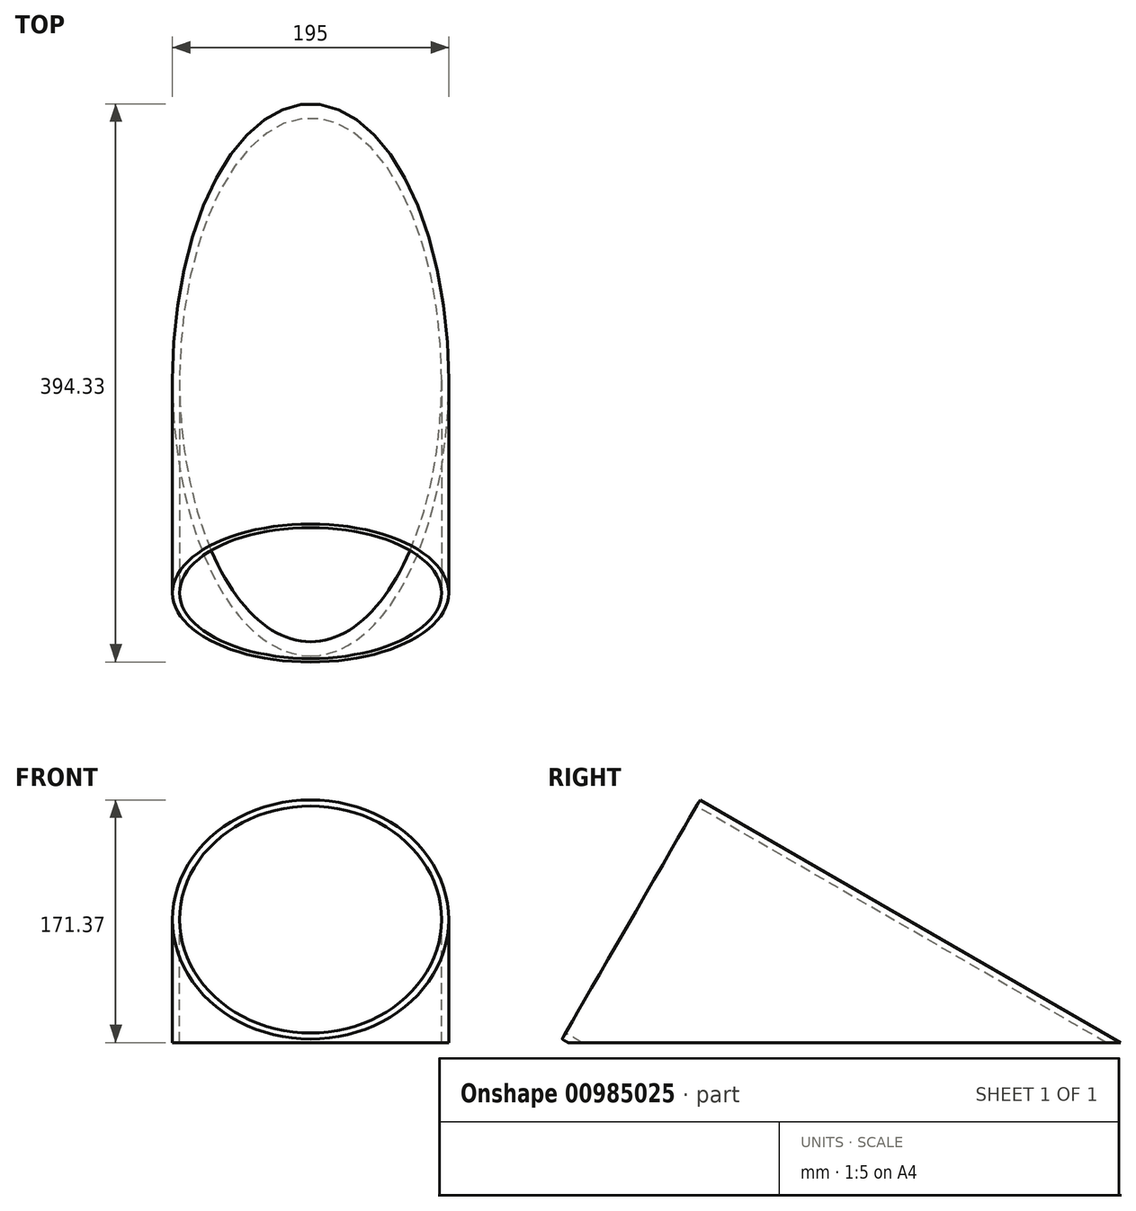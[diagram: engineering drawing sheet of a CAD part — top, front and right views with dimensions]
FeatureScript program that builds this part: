
annotation { "Feature Type Name" : "Feature", "Feature Type Description" : "" }
export const myFeature = defineFeature(function(context is Context, id is Id, definition is map)
    precondition{}
    {
        {
            var Q0;
            Q0=qCreatedBy(makeId("Top.planeOp"),FACE);
            var sketch = newSketch(context, id + "F0", { "sketchPlane" : qUnion([Q0])});
            skLineSegment(sketch, "E0", {"start": v(-54.49, 0) * mm, "end": v(52.75, 0) * mm});
            skSolve(sketch);
        }
        {
            var Q0;
            Q0=qCreatedBy(makeId("Top.planeOp"),FACE);
            var Q1;
            Q1=sQuery(id+"F0.wireOp",EDGE,"E0");
            cPlane(context, id + "F1", {"entities" : qUnion([Q0, Q1]), "cplaneType" : CPlaneType.LINE_ANGLE, "offset" : 25 * mm, "angle" : 60 * degree, "width" : 150 * mm, "height" : 150 * mm});
        }
        {
            var Q0;
            Q0=qCreatedBy(id+"F1.planeOp",FACE);
            var sketch = newSketch(context, id + "F2", { "sketchPlane" : qUnion([Q0])});
            skCircle(sketch, "E1", {"center": v(0, 97.5) * mm, "radius": 97.5 * mm});
            skCircle(sketch, "E2", {"center": v(0, 97.5) * mm, "radius": 92.5 * mm});
            skLineSegment(sketch, "E3", {"start": v(0, 0) * mm, "end": v(0, 97.5) * mm});
            skSolve(sketch);
        }
        {
            var Q0;
            Q0=makeQuery(id+"F2.imprint","IMPRINT",FACE,{"disambiguationData":[TD([[makeQuery(id+"F2.imprint","IMPRINT",EDGE,{"derivedFrom":sQuery(id+"F2.wireOp",EDGE,"E1")}),1.0]])]});
            var Q1;
            Q1=qCreatedBy(makeId("Top.planeOp"),FACE);
            extrude(context, id + "F3", {"entities" : qUnion([Q0]), "endBound" : BoundingType.UP_TO_SURFACE, "depth" : 25 * mm, "endBoundEntityFace" : qUnion([Q1]), "offsetDistance" : 25 * mm, "hasSecondDirection" : true, "secondDirectionOppositeDirection" : true, "secondDirectionDepth" : 5 * mm});
        }
    });
